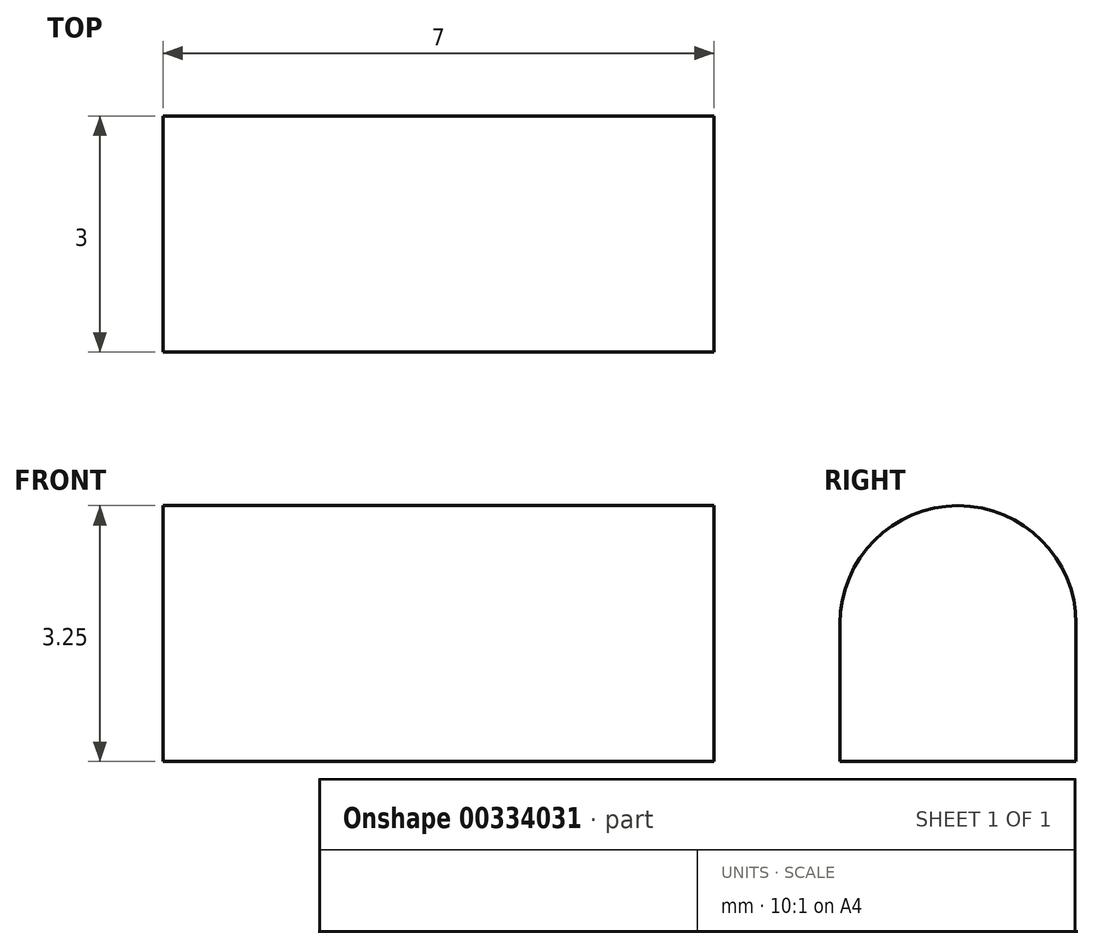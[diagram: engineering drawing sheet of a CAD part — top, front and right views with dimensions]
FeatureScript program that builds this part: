
annotation { "Feature Type Name" : "Feature", "Feature Type Description" : "" }
export const myFeature = defineFeature(function(context is Context, id is Id, definition is map)
    precondition{}
    {
        {
            var Q0;
            Q0=qCreatedBy(makeId("Top.planeOp"),FACE);
            var sketch = newSketch(context, id + "F0", { "sketchPlane" : qUnion([Q0])});
            skLineSegment(sketch, "E0.bottom", {"start": v(3.5, -1.5) * mm, "end": v(-3.5, -1.5) * mm});
            skLineSegment(sketch, "E0.top", {"start": v(3.5, 1.5) * mm, "end": v(-3.5, 1.5) * mm});
            skLineSegment(sketch, "E0.left", {"start": v(3.5, -1.5) * mm, "end": v(3.5, 1.5) * mm});
            skLineSegment(sketch, "E0.right", {"start": v(-3.5, -1.5) * mm, "end": v(-3.5, 1.5) * mm});
            skPoint(sketch, "E0.middle", {"position": v(0, 0) * mm});
            skSolve(sketch);
        }
        {
            var Q0;
            Q0=makeQuery(id+"F0.imprint","IMPRINT",FACE,{"disambiguationData":[TD([[makeQuery(id+"F0.imprint","IMPRINT",EDGE,{"derivedFrom":sQuery(id+"F0.wireOp",EDGE,"E0.bottom")}),-1.0]])]});
            extrude(context, id + "F1", {"entities" : qUnion([Q0]), "depth" : 3.25 * mm});
        }
        {
            var Q0;
            Q0=makeQuery(id+"F1.opExtrude","CAP_EDGE",EDGE,{"disambiguationData":[OSD([sQuery(id+"F0.wireOp",EDGE,"E0.bottom")])],"isStart":false});
            var Q1;
            Q1=makeQuery(id+"F1.opExtrude","CAP_EDGE",EDGE,{"disambiguationData":[OSD([sQuery(id+"F0.wireOp",EDGE,"E0.top")])],"isStart":false});
            fillet(context, id + "F2", {"entities" : qUnion([Q0, Q1]), "radius" : 1.5 * mm, "tangentPropagation" : true, "allowEdgeOverflow" : false});
        }
    });
